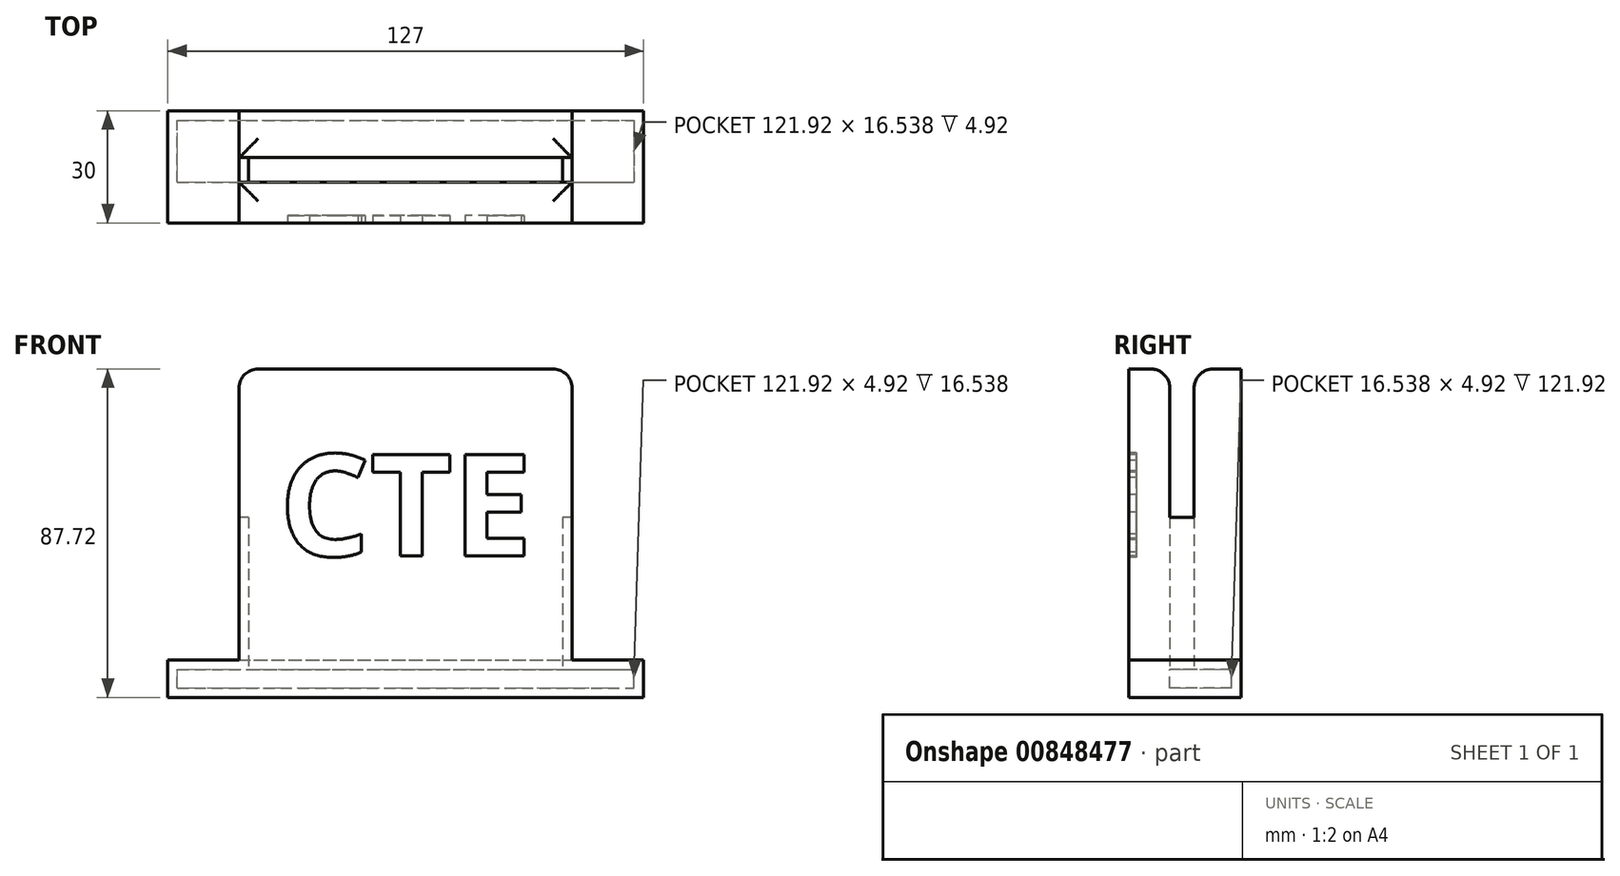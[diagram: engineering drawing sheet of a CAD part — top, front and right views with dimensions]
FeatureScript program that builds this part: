
annotation { "Feature Type Name" : "Feature", "Feature Type Description" : "" }
export const myFeature = defineFeature(function(context is Context, id is Id, definition is map)
    precondition{}
    {
        {
            var Q0;
            Q0=qCreatedBy(makeId("Top.planeOp"),FACE);
            var sketch = newSketch(context, id + "F0", { "sketchPlane" : qUnion([Q0])});
            skLineSegment(sketch, "E0", {"start": v(-62.53, 0) * mm, "end": v(-62.53, 30) * mm});
            skLineSegment(sketch, "E1", {"start": v(-62.53, 30) * mm, "end": v(64.47, 30) * mm});
            skLineSegment(sketch, "E2", {"start": v(64.47, 30) * mm, "end": v(64.47, 0) * mm});
            skLineSegment(sketch, "E3", {"start": v(-62.53, 0) * mm, "end": v(64.47, 0) * mm});
            skSolve(sketch);
        }
        {
            var Q0;
            Q0=qSketchRegion(id+"F0",true);
            extrude(context, id + "F1", {"entities" : qUnion([Q0]), "oppositeDirection" : true, "depth" : 10 * mm});
        }
        {
            var Q0;
            Q0=qCreatedBy(makeId("Front.planeOp"),FACE);
            var sketch = newSketch(context, id + "F2", { "sketchPlane" : qUnion([Q0])});
            skLineSegment(sketch, "E4", {"start": v(-43.5, 38.1) * mm, "end": v(45.4, 38.1) * mm});
            skLineSegment(sketch, "E5", {"start": v(-43.5, 38.1) * mm, "end": v(-43.5, 0) * mm});
            skLineSegment(sketch, "E6", {"start": v(45.4, 38.1) * mm, "end": v(45.4, 0) * mm});
            skLineSegment(sketch, "E7", {"start": v(-43.5, 0) * mm, "end": v(45.4, 0) * mm});
            skSolve(sketch);
        }
        {
            var Q0;
            Q0=makeQuery(id+"F2.imprint","IMPRINT",FACE,{"disambiguationData":[TD([[makeQuery(id+"F2.imprint","IMPRINT",EDGE,{"derivedFrom":sQuery(id+"F2.wireOp",EDGE,"E4")}),-1.0]])]});
            extrude(context, id + "F3", {"entities" : qUnion([Q0]), "operationType" : NewBodyOperationType.ADD, "oppositeDirection" : true, "depth" : 29.97 * mm});
        }
        {
            var Q0;
            Q0=makeQuery(id+"F3.opExtrude","SWEPT_FACE",FACE,{"disambiguationData":[OSD([sQuery(id+"F2.wireOp",EDGE,"E4")])]});
            shell(context, id + "F4", {"entities" : qUnion([Q0]), "thickness" : 2.54 * mm});
        }
        {
            var Q0;
            {var subQ0=sQuery(id+"F2.wireOp",EDGE,"E4");Q0=makeQuery(id+"FXIdfenQM2DYknQ_1.boolean.opBoolean","MERGE",FACE,{"derivedFrom":[makeQuery(id+"F4.opShell","OFFSET_FACE",FACE,{"disambiguationData":[OSD([subQ0,sQuery(id+"F2.wireOp",EDGE,"E5"),sQuery(id+"F2.wireOp",EDGE,"E6"),sQuery(id+"F2.wireOp",EDGE,"E7")])]}),makeQuery(id+"FXIdfenQM2DYknQ_1.opExtrude","SWEPT_FACE",FACE,{"disambiguationData":[OSD([subQ0]),TDD([makeQuery(id+"FuGBquXPF5WmrCm_1.imprint","IMPRINT",EDGE,{"derivedFrom":makeQuery(id+"F4.opShell","OFFSET_EDGE",EDGE,{"disambiguationData":[OSD([subQ0]),TDD([makeQuery(id+"F3.opExtrude","CAP_EDGE",EDGE,{"disambiguationData":[OSD([subQ0])],"isStart":false})])]})})])]})]});}
            extrude(context, id + "F5", {"entities" : qUnion([Q0]), "operationType" : NewBodyOperationType.ADD, "depth" : 10 * mm});
        }
        {
            var Q0;
            {var subQ0=sQuery(id+"F2.wireOp",EDGE,"E4");Q0=makeQuery(id+"FXIdfenQM2DYknQ_1.boolean.opBoolean","MERGE",FACE,{"derivedFrom":[makeQuery(id+"F4.opShell","OFFSET_FACE",FACE,{"disambiguationData":[OSD([sQuery(id+"F0.wireOp",EDGE,"E3"),subQ0,sQuery(id+"F2.wireOp",EDGE,"E5"),sQuery(id+"F2.wireOp",EDGE,"E6"),sQuery(id+"F2.wireOp",EDGE,"E7")])]}),makeQuery(id+"FXIdfenQM2DYknQ_1.opExtrude","SWEPT_FACE",FACE,{"disambiguationData":[OSD([subQ0]),TDD([makeQuery(id+"FuGBquXPF5WmrCm_1.imprint","IMPRINT",EDGE,{"derivedFrom":makeQuery(id+"F4.opShell","OFFSET_EDGE",EDGE,{"disambiguationData":[OSD([subQ0]),TDD([makeQuery(id+"F3.opExtrude","CAP_EDGE",EDGE,{"disambiguationData":[OSD([subQ0])],"isStart":true})])]})})])]})]});}
            extrude(context, id + "F6", {"entities" : qUnion([Q0]), "operationType" : NewBodyOperationType.ADD, "depth" : 8.38 * mm});
        }
        {
            var Q0;
            {var subQ0=sQuery(id+"F2.wireOp",EDGE,"E4");Q0=makeQuery(id+"F6.boolean.opBoolean","MERGE",FACE,{"derivedFrom":[makeQuery(id+"F5.boolean.opBoolean","MERGE",FACE,{"derivedFrom":[makeQuery(id+"F3.opExtrude","SWEPT_FACE",FACE,{"disambiguationData":[OSD([subQ0])]}),makeQuery(id+"F5.opExtrude","SWEPT_FACE",FACE,{"disambiguationData":[OSD([subQ0])]})]}),makeQuery(id+"F6.opExtrude","SWEPT_FACE",FACE,{"disambiguationData":[OSD([subQ0])]})]});}
            var sketch = newSketch(context, id + "F7", { "sketchPlane" : qUnion([Q0])});
            skLineSegment(sketch, "E8", {"start": v(-40.96, 10.92) * mm, "end": v(-43.5, 10.92) * mm});
            skLineSegment(sketch, "E9", {"start": v(-40.96, 17.43) * mm, "end": v(-43.5, 17.43) * mm});
            skLineSegment(sketch, "E10", {"start": v(42.86, 17.43) * mm, "end": v(45.4, 17.43) * mm});
            skLineSegment(sketch, "E11", {"start": v(42.86, 10.92) * mm, "end": v(45.4, 10.92) * mm});
            skSolve(sketch);
        }
        {
            var Q0;
            {var subQ3=sQuery(id+"F7.wireOp",EDGE,"E9");Q0=makeQuery(id+"F7.imprint","IMPRINT",FACE,{"disambiguationData":[TD([[makeQuery(id+"F7.imprint","IMPRINT",EDGE,{"derivedFrom":subQ3}),-1.0]])]});}
            var Q1;
            {var subQ3=sQuery(id+"F7.wireOp",EDGE,"E8");Q1=makeQuery(id+"F7.imprint","IMPRINT",FACE,{"disambiguationData":[TD([[makeQuery(id+"F7.imprint","IMPRINT",EDGE,{"derivedFrom":subQ3}),1.0]])]});}
            extrude(context, id + "F8", {"entities" : qUnion([Q0, Q1]), "operationType" : NewBodyOperationType.ADD, "depth" : 39.62 * mm});
        }
        {
            var Q0;
            {var subQ0=sQuery(id+"F2.wireOp",EDGE,"E4");var subQ2=sQuery(id+"F2.wireOp",EDGE,"E5");var subQ4=sQuery(id+"F0.wireOp",EDGE,"E3");var subQ7=sQuery(id+"F0.wireOp",EDGE,"E0");var subQ10=sQuery(id+"F2.wireOp",EDGE,"E6");var subQ11=makeQuery(id+"F3.opExtrude","CAP_EDGE",EDGE,{"disambiguationData":[OSD([subQ0])],"isStart":true});Q0=makeQuery(id+"F78bqgrH38Iybbp_1.boolean.opBoolean","SPLIT",FACE,{"disambiguationData":[TD([makeQuery(id+"F1.opExtrude","SWEPT_FACE",FACE,{"disambiguationData":[OSD([subQ7])]})])],"derivedFrom":makeQuery(id+"F8.boolean.opBoolean","MERGE",FACE,{"derivedFrom":[makeQuery(id+"F3.boolean.opBoolean","MERGE",FACE,{"derivedFrom":[makeQuery(id+"F1.opExtrude","SWEPT_FACE",FACE,{"disambiguationData":[OSD([subQ4])]}),makeQuery(id+"F3.opExtrude","CAP_FACE",FACE,{"disambiguationData":[OSD([subQ0,subQ2,subQ10,sQuery(id+"F2.wireOp",EDGE,"E7")])],"isStart":true})]}),makeQuery(id+"F8.opExtrude","SWEPT_FACE",FACE,{"disambiguationData":[OSD([subQ0]),TDD([makeQuery(id+"F7.imprint","IMPRINT",EDGE,{"derivedFrom":subQ11})])]})]})});}
            var sketch = newSketch(context, id + "F9", { "sketchPlane" : qUnion([Q0])});
            skSolve(sketch);
        }
        {
            var Q0;
            {var subQ0=sQuery(id+"F2.wireOp",EDGE,"E4");var subQ1=sQuery(id+"F2.wireOp",EDGE,"E5");var subQ2=makeQuery(id+"F3.opExtrude","SWEPT_EDGE",EDGE,{"disambiguationData":[OSD([subQ0,subQ1])]});Q0=makeQuery(id+"F8.opExtrude","CAP_EDGE",EDGE,{"disambiguationData":[OSD([subQ0,subQ1]),TDD([makeQuery(id+"F7.imprint","IMPRINT",EDGE,{"disambiguationData":[TD([[makeQuery(id+"F7.imprint","INTERSECT",VERTEX,{"derivedFrom":[subQ2,makeQuery(id+"F3.opExtrude","CAP_EDGE",EDGE,{"disambiguationData":[OSD([subQ0])],"isStart":true})]}),1.0]])],"derivedFrom":subQ2})])],"isStart":false});}
            var Q1;
            Q1=makeQuery(id+"F8.opExtrude","CAP_EDGE",EDGE,{"disambiguationData":[OSD([sQuery(id+"F2.wireOp",EDGE,"E4"),sQuery(id+"F7.wireOp",EDGE,"E8"),sQuery(id+"F7.wireOp",EDGE,"E11")])],"isStart":false});
            var Q2;
            Q2=makeQuery(id+"F8.opExtrude","CAP_EDGE",EDGE,{"disambiguationData":[OSD([sQuery(id+"F2.wireOp",EDGE,"E4"),sQuery(id+"F7.wireOp",EDGE,"E9"),sQuery(id+"F7.wireOp",EDGE,"E10")])],"isStart":false});
            var Q3;
            {var subQ0=sQuery(id+"F2.wireOp",EDGE,"E4");var subQ1=sQuery(id+"F2.wireOp",EDGE,"E6");var subQ2=makeQuery(id+"F3.opExtrude","SWEPT_EDGE",EDGE,{"disambiguationData":[OSD([subQ0,subQ1])]});Q3=makeQuery(id+"F8.opExtrude","CAP_EDGE",EDGE,{"disambiguationData":[OSD([subQ0,subQ1]),TDD([makeQuery(id+"F7.imprint","IMPRINT",EDGE,{"disambiguationData":[TD([[makeQuery(id+"F7.imprint","INTERSECT",VERTEX,{"derivedFrom":[subQ2,makeQuery(id+"F3.opExtrude","CAP_EDGE",EDGE,{"disambiguationData":[OSD([subQ0])],"isStart":false})]}),-1.0]])],"derivedFrom":subQ2})])],"isStart":false});}
            var Q4;
            {var subQ0=sQuery(id+"F2.wireOp",EDGE,"E4");var subQ1=sQuery(id+"F2.wireOp",EDGE,"E6");var subQ2=makeQuery(id+"F3.opExtrude","SWEPT_EDGE",EDGE,{"disambiguationData":[OSD([subQ0,subQ1])]});Q4=makeQuery(id+"F8.opExtrude","CAP_EDGE",EDGE,{"disambiguationData":[OSD([subQ0,subQ1]),TDD([makeQuery(id+"F7.imprint","IMPRINT",EDGE,{"disambiguationData":[TD([[makeQuery(id+"F7.imprint","INTERSECT",VERTEX,{"derivedFrom":[subQ2,makeQuery(id+"F3.opExtrude","CAP_EDGE",EDGE,{"disambiguationData":[OSD([subQ0])],"isStart":true})]}),1.0]])],"derivedFrom":subQ2})])],"isStart":false});}
            var Q5;
            {var subQ0=sQuery(id+"F2.wireOp",EDGE,"E4");var subQ1=sQuery(id+"F2.wireOp",EDGE,"E5");var subQ2=makeQuery(id+"F3.opExtrude","SWEPT_EDGE",EDGE,{"disambiguationData":[OSD([subQ0,subQ1])]});Q5=makeQuery(id+"F8.opExtrude","CAP_EDGE",EDGE,{"disambiguationData":[OSD([subQ0,subQ1]),TDD([makeQuery(id+"F7.imprint","IMPRINT",EDGE,{"disambiguationData":[TD([[makeQuery(id+"F7.imprint","INTERSECT",VERTEX,{"derivedFrom":[subQ2,makeQuery(id+"F3.opExtrude","CAP_EDGE",EDGE,{"disambiguationData":[OSD([subQ0])],"isStart":false})]}),-1.0]])],"derivedFrom":subQ2})])],"isStart":false});}
            fillet(context, id + "F10", {"entities" : qUnion([Q0, Q1, Q2, Q3, Q4, Q5]), "radius" : 5.08 * mm, "tangentPropagation" : true, "allowEdgeOverflow" : false});
        }
        {
            var Q0;
            {var subQ0=sQuery(id+"F0.wireOp",EDGE,"E3");Q0=makeQuery(id+"F9.imprint","IMPRINT",FACE,{"disambiguationData":[TD([[makeQuery(id+"F9.imprint","IMPRINT",EDGE,{"derivedFrom":makeQuery(id+"F1.opExtrude","CAP_EDGE",EDGE,{"disambiguationData":[OSD([subQ0])],"isStart":false})}),1.0]])]});}
            var sketch = newSketch(context, id + "F11", { "sketchPlane" : qUnion([Q0])});
            skText(sketch, "E12", { "text": "CTE", "fontName": "OpenSans-Bold.ttf"});
            const initialGuessF11  = {"E12": [-0.03281, 0.02774, 1, 0, 0.02739]};
            skSetInitialGuess(sketch, initialGuessF11);
            skSolve(sketch);
        }
        {
            var Q0;
            Q0 = qSketchRegion(id + "F11", true);
            extrude(context, id + "F12", {"entities" : qUnion([Q0]), "operationType" : NewBodyOperationType.REMOVE, "oppositeDirection" : true, "depth" : 2.03 * mm, "offsetDistance" : 25.4 * mm});
        }
    });
